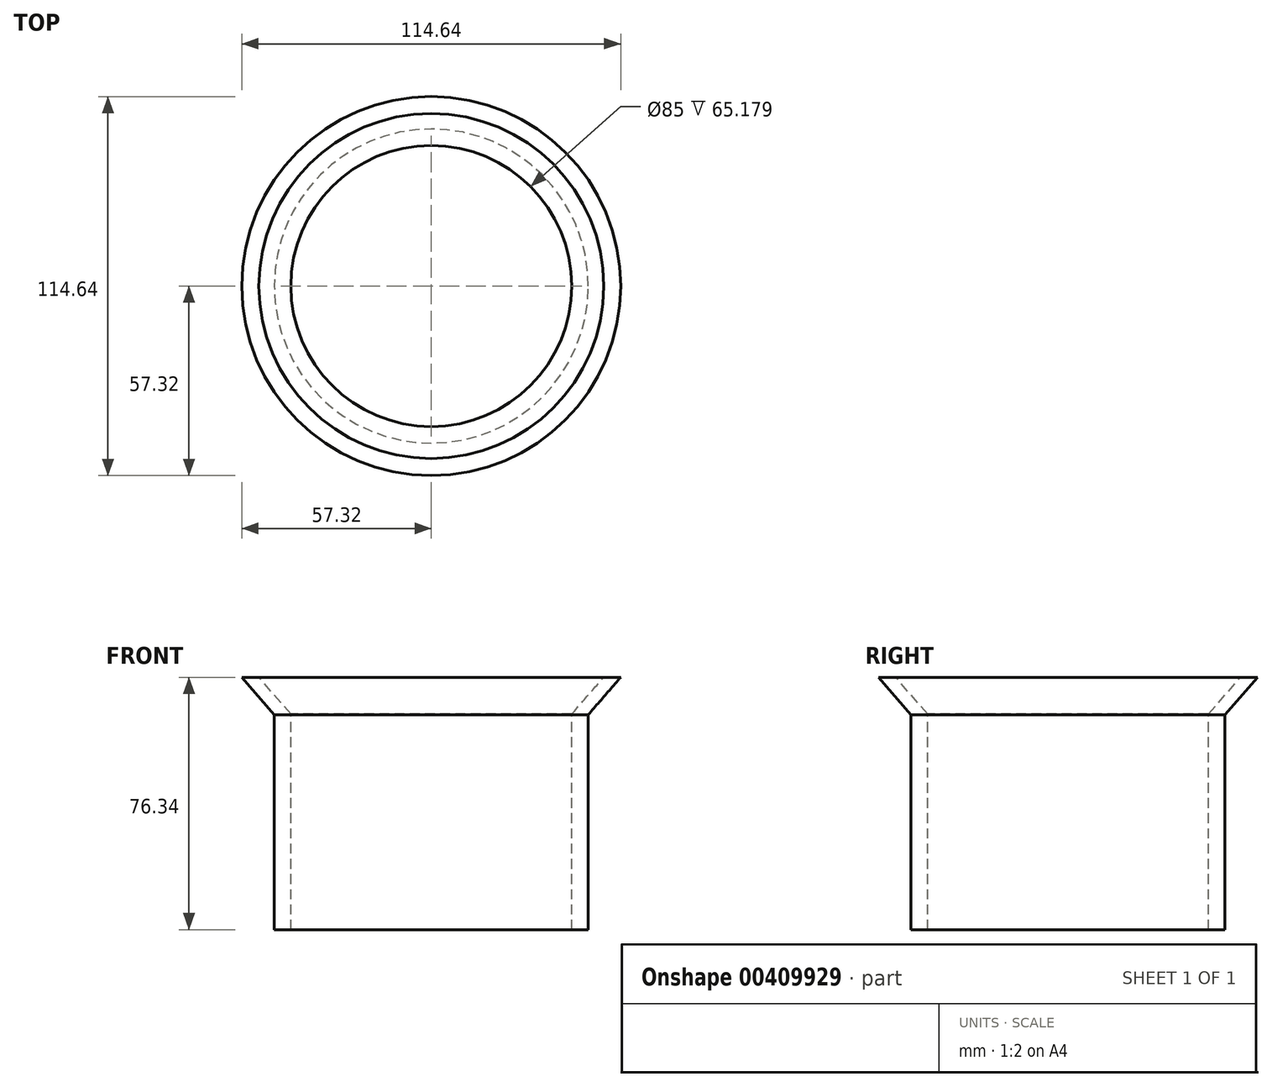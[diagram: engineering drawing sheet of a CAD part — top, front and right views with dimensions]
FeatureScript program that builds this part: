
annotation { "Feature Type Name" : "Feature", "Feature Type Description" : "" }
export const myFeature = defineFeature(function(context is Context, id is Id, definition is map)
    precondition{}
    {
        {
            var Q0;
            Q0=qCreatedBy(makeId("Front.planeOp"),FACE);
            var sketch = newSketch(context, id + "F0", { "sketchPlane" : qUnion([Q0])});
            skLineSegment(sketch, "E0", {"start": v(0, 38.64) * mm, "end": v(0, -37.08) * mm, "construction": true});
            skLineSegment(sketch, "E1", {"start": v(42.5, 11.67) * mm, "end": v(42.5, -53.5) * mm});
            skLineSegment(sketch, "E2", {"start": v(42.5, -53.5) * mm, "end": v(47.5, -53.5) * mm});
            skLineSegment(sketch, "E3", {"start": v(47.5, -53.5) * mm, "end": v(47.5, 11.5) * mm});
            skLineSegment(sketch, "E4", {"start": v(42.5, 11.67) * mm, "end": v(52.17, 22.83) * mm});
            skLineSegment(sketch, "E5", {"start": v(47.5, 11.5) * mm, "end": v(57.32, 22.83) * mm});
            skLineSegment(sketch, "E6", {"start": v(52.17, 22.83) * mm, "end": v(57.32, 22.83) * mm});
            skSolve(sketch);
        }
        {
            var Q0;
            Q0 = qSketchRegion(id + "F0", true);
            var Q1;
            Q1=sQuery(id+"F0.wireOp",EDGE,"E0");
            revolve(context, id + "F1", {"entities" : qUnion([Q0]), "axis" : qUnion([Q1]), "revolveType" : RevolveType.FULL});
        }
    });
